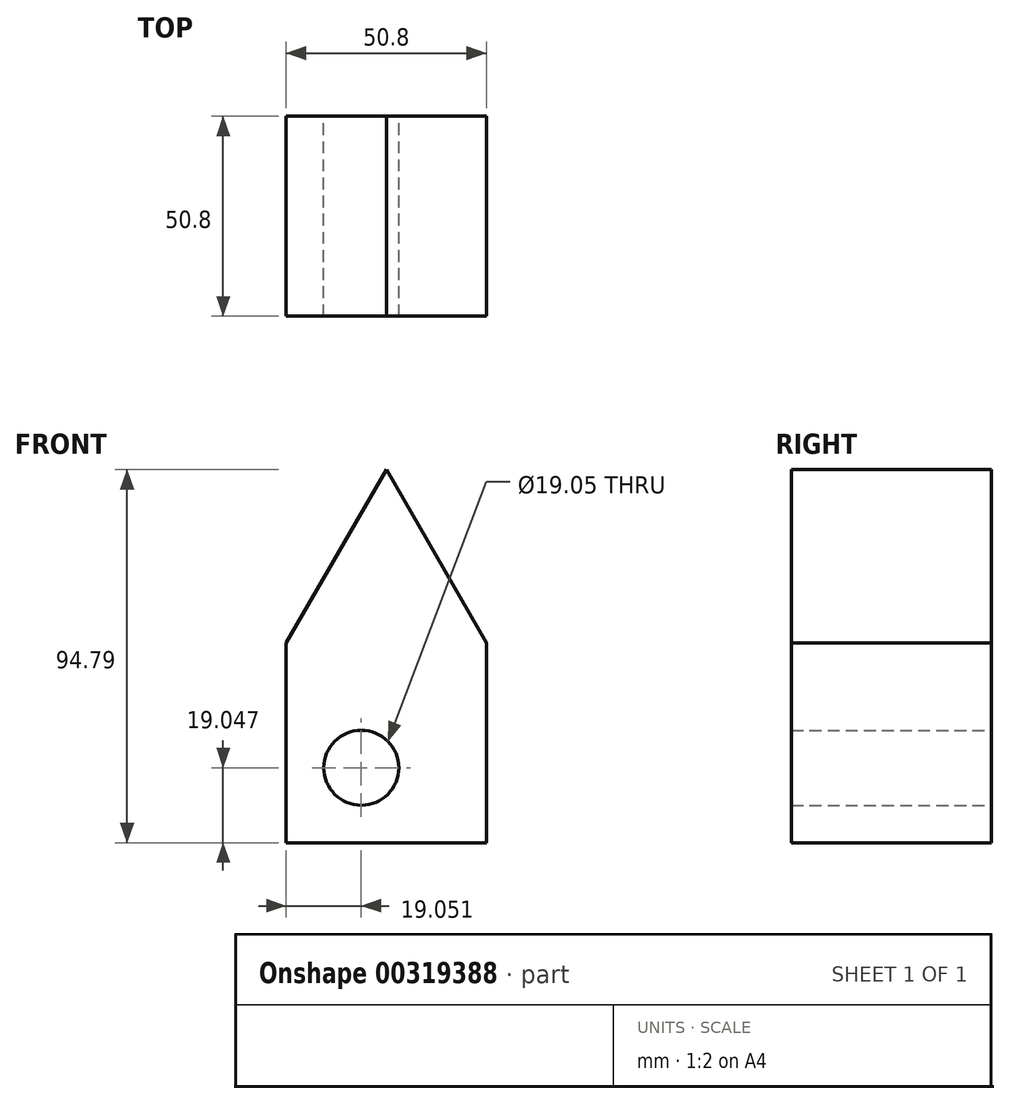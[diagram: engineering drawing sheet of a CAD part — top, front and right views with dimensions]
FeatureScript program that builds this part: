
annotation { "Feature Type Name" : "Feature", "Feature Type Description" : "" }
export const myFeature = defineFeature(function(context is Context, id is Id, definition is map)
    precondition{}
    {
        {
            var Q0;
            Q0=qCreatedBy(makeId("Front.planeOp"),FACE);
            var sketch = newSketch(context, id + "F0", { "sketchPlane" : qUnion([Q0])});
            skLineSegment(sketch, "E0.top", {"start": v(-15.39, -40.44) * mm, "end": v(35.41, -40.44) * mm});
            skLineSegment(sketch, "E0.left", {"start": v(-15.39, 10.36) * mm, "end": v(-15.39, -40.44) * mm});
            skLineSegment(sketch, "E0.right", {"start": v(35.41, 10.36) * mm, "end": v(35.41, -40.44) * mm});
            skLineSegment(sketch, "E1", {"start": v(-15.39, 10.36) * mm, "end": v(10.01, 54.35) * mm});
            skLineSegment(sketch, "E2", {"start": v(35.41, 10.36) * mm, "end": v(10.01, 54.35) * mm});
            skCircle(sketch, "E3", {"center": v(3.66, -21.4) * mm, "radius": 9.53 * mm});
            skSolve(sketch);
        }
        {
            var Q0;
            Q0 = qSketchRegion(id + "F0", true);
            extrude(context, id + "F1", {"entities" : qUnion([Q0]), "depth" : 50.8 * mm});
        }
    });
